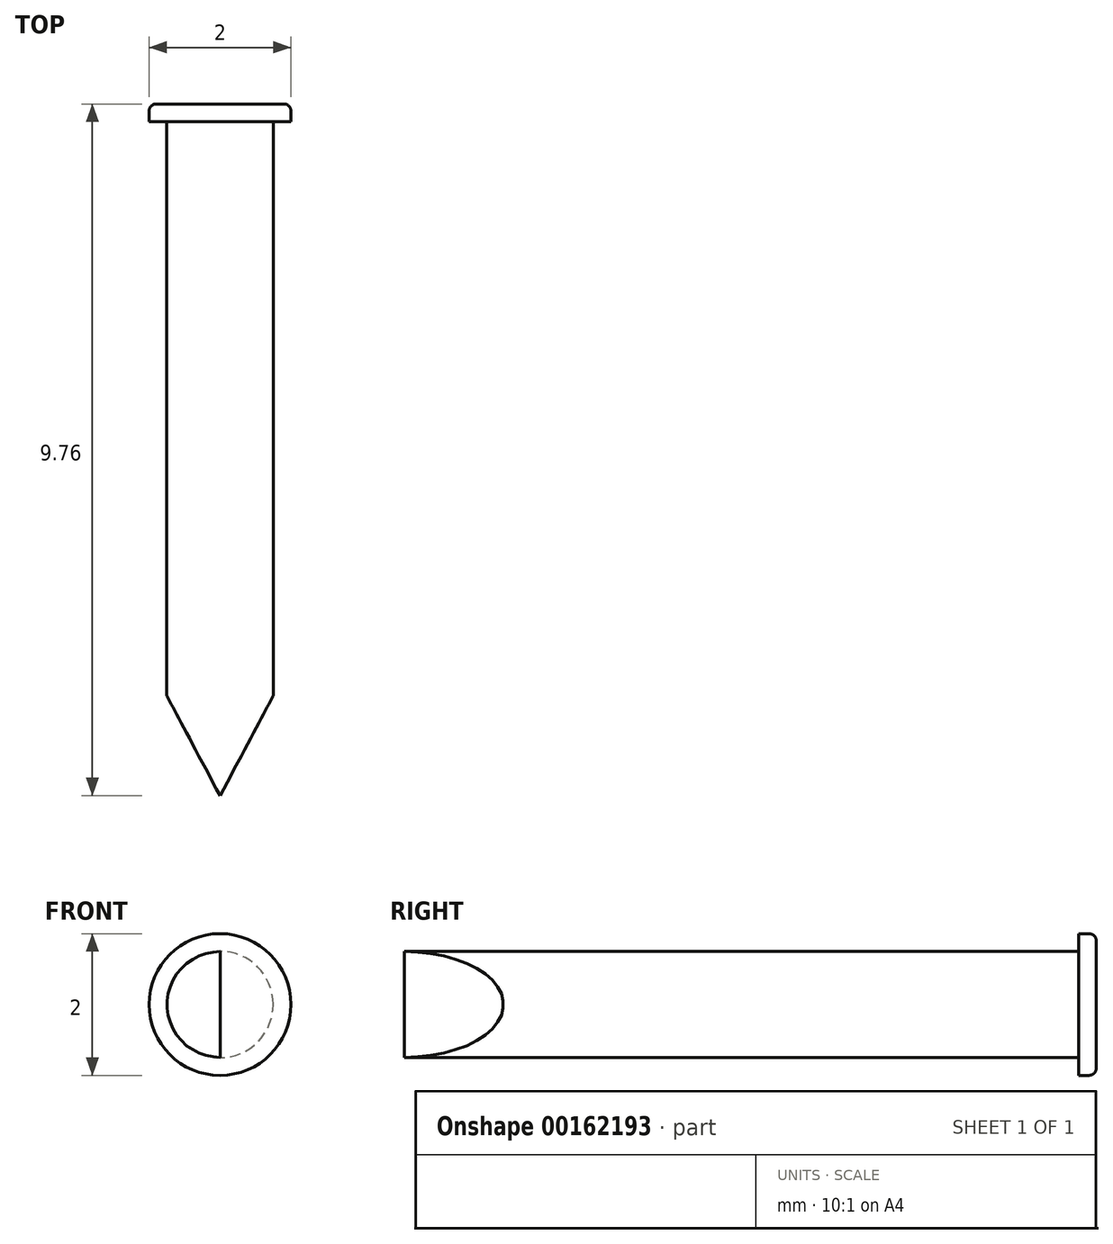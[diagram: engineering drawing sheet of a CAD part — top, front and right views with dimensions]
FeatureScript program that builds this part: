
annotation { "Feature Type Name" : "Feature", "Feature Type Description" : "" }
export const myFeature = defineFeature(function(context is Context, id is Id, definition is map)
    precondition{}
    {
        {
            var Q0;
            Q0=qCreatedBy(makeId("Front.planeOp"),FACE);
            var sketch = newSketch(context, id + "F0", { "sketchPlane" : qUnion([Q0])});
            skCircle(sketch, "E0", {"center": v(0, 0) * mm, "radius": 0.75 * mm});
            skCircle(sketch, "E1", {"center": v(0, 0) * mm, "radius": 1 * mm});
            skSolve(sketch);
        }
        {
            var Q0;
            Q0=makeQuery(id+"F0.imprint","IMPRINT",FACE,{"disambiguationData":[TD([[makeQuery(id+"F0.imprint","IMPRINT",EDGE,{"derivedFrom":sQuery(id+"F0.wireOp",EDGE,"E0")}),1.0]])]});
            extrude(context, id + "F1", {"entities" : qUnion([Q0]), "depth" : 10 * mm});
        }
        {
            var Q0;
            Q0=makeQuery(id+"F0.imprint","IMPRINT",FACE,{"disambiguationData":[TD([[makeQuery(id+"F0.imprint","IMPRINT",EDGE,{"derivedFrom":sQuery(id+"F0.wireOp",EDGE,"E0")}),-1.0]])]});
            extrude(context, id + "F2", {"entities" : qUnion([Q0]), "operationType" : NewBodyOperationType.ADD, "depth" : 0.25 * mm});
        }
        {
            var Q0;
            Q0=makeQuery(id+"F2.opExtrude","CAP_EDGE",EDGE,{"disambiguationData":[OSD([sQuery(id+"F0.wireOp",EDGE,"E1")])],"isStart":true});
            fillet(context, id + "F3", {"entities" : qUnion([Q0]), "radius" : 0.1 * mm, "tangentPropagation" : true, "allowEdgeOverflow" : false});
        }
        {
            var Q0;
            Q0=qCreatedBy(makeId("Top.planeOp"),FACE);
            var sketch = newSketch(context, id + "F4", { "sketchPlane" : qUnion([Q0])});
            skLineSegment(sketch, "E2.bottom", {"start": v(-1, -10.46) * mm, "end": v(1, -10.46) * mm});
            skLineSegment(sketch, "E2.top", {"start": v(-1, -8.26) * mm, "end": v(-0.8, -8.26) * mm});
            skLineSegment(sketch, "E2.left", {"start": v(-1, -10.46) * mm, "end": v(-1, -8.26) * mm});
            skLineSegment(sketch, "E2.right", {"start": v(1, -10.46) * mm, "end": v(1, -8.26) * mm});
            skLineSegment(sketch, "E3", {"start": v(-0.8, -8.26) * mm, "end": v(0, -9.76) * mm});
            skLineSegment(sketch, "E4", {"start": v(0, -9.76) * mm, "end": v(0.8, -8.26) * mm});
            skLineSegment(sketch, "E5.trimOffspring", {"start": v(0.8, -8.26) * mm, "end": v(1, -8.26) * mm});
            skSolve(sketch);
        }
        {
            var Q0;
            Q0=makeQuery(id+"F4.imprint","IMPRINT",FACE,{"disambiguationData":[TD([[makeQuery(id+"F4.imprint","IMPRINT",EDGE,{"derivedFrom":sQuery(id+"F4.wireOp",EDGE,"E2.bottom")}),1.0]])]});
            extrude(context, id + "F5", {"entities" : qUnion([Q0]), "operationType" : NewBodyOperationType.REMOVE, "depth" : 25 * mm, "hasSecondDirection" : true, "secondDirectionOppositeDirection" : true, "secondDirectionDepth" : 25 * mm});
        }
    });
